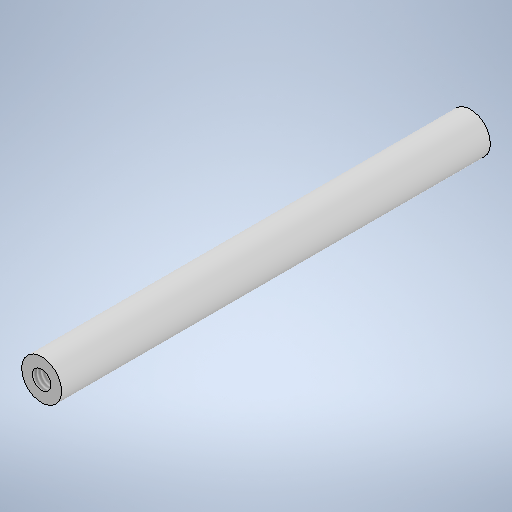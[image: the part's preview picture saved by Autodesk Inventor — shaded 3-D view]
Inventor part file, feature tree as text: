
AUTODESK INVENTOR PART (.ipt)
format: ipt  version: 2025 (Build 290162010, 162A)  size: 250,880 bytes
history: native  units: mm
features: sketch x3, hole x2, extrude x1
ambient origin geometry x8: Origin, YZ Plane, XZ Plane, XY Plane, X Axis, Y Axis, Z Axis, Center Point
bodies: Solid1 (feature_tree)
feature tree (6):
  extrude  "Extrusion1"  Depth=75.0mm TaperAngle=0.0deg
  hole  "Hole1"  [1 undecoded]
  hole  "Hole2"  [1 undecoded]
  sketch  "Sketch1"  dims[d0=7.0mm d1=75.0mm d2=0.0mm]
  sketch  "Sketch2"  dims[d3=3.242mm d4=10.0mm d5=4.0mm d6=2.0mm d7=90.0deg d8=10.0mm d9=0.0mm]
  sketch  "Sketch3"  dims[d10=3.242mm d11=10.0mm d12=4.0mm d13=2.0mm d14=90.0deg d15=10.0mm d16=0.0mm]
note: 2 required parameter values undecoded (feature->parameter linkage not recoverable at this tier; creation-order binding heuristic only, values carry confidence <= 0.55)
